# Revit family: Sirena electronica con foco EN 54-23 bajo consumo_Aguilera Electronica
name_source: partatom
category: Dispositivos de alarma de incendios
units: mm (PartAtom-declared; Revit-internal decimal feet)

## family parameters
Anfitrión = Cara
Compartido = No
Corte con vacíos al cargar = No
Cota de conector redondo = Diámetro de uso
Mantener orientación de anotación = Sí
Número OmniClass = 23.85.30.21.14.11
Punto de cálculo de habitación = No
Tipo de pieza = Normal
Título OmniClass = Concentration Detection Bells and Sounders

## types (1)
- Sirena electronica con foco EN 54-23 bajo consumo
    Altura 1 = 10 mm  [stored 0.0328084 ft]
    Altura 2 = 53 mm  [stored 0.173885 ft]
    Altura 3 = 17 mm
    Descripción = Sirena acústica con foco de bajo consumo para uso interior certificada EN 54-3 y EN 54-23. La sirena puede configurarse como elemento óptico-acústico (luz+sonido) o solo óptico.
    Diámetro tubo = 20 mm  [stored 0.0656168 ft]
    Elevación por defecto = 0 mm  [stored 0 ft]
    Fabricante = Aguilera Electrónica
    Foco = Sí
    Interior = Sí
    Modelo = AE/V-ASF23
    Sirena = No
    Símbolo = Sí
    Símbolo texto modelo = Sí
    URL = https://aguilera.es

note: [stored X ft] marks values corroborated as IEEE doubles in the binary element streams (Revit-internal decimal feet)
